# Revit family: ADSK_Фундамент_Монолитный_КолоннаМеталлическая_с_подливкой
name_source: partatom
category: Фундамент несущей конструкции
units: mm (PartAtom-declared; Revit-internal decimal feet)

## family parameters
Всегда вертикально = Да
Заглушка = Нет
Материал для поведения модели = Бетон
На основе рабочей плоскости = Нет
Общий = Нет
При загрузке вырезать с полостями = Нет

## types (5) — shared parameters
ADSK_Версия Revit = 2021
ADSK_Версия семейства = 1.1
ADSK_Масса элемента = 0.00 кг
ADSK_Основной материал элемента = Бетон
Материал несущих конструкций = <По категории>
Материал подливки = <По категории>
Подколонник_Ширина = 400 мм
Подливка = Да
ТВ1 = Болт фундаментный_Тип 1_ГОСТ 24379.1-2012
ТВ2 = Болт фундаментный_Тип 5_ГОСТ 24379.1-2012
Уступ 2_Высота = 200 мм
Уступ 3_Высота = 200 мм
zero-valued in all types: Толщина фундамента

## per-type parameters (varying)
| type | ADSK_Наименование | Длина | Плита_Количество уступов | Подколонник_Высота | Подколонник_Длина | Подливка_Длина | Подливка_ширина | Расч_Плита_Количество уступов | Расч_Уступ 2_Высота | Расч_Уступ 2_Длина | Расч_Уступ 2_Ширина | Расч_Уступ 3_Высота | Расч_Уступ 3_Длина | Расч_Уступ 3_Ширина | Смещение_Уступ 2 | Смещение_Уступ 3 | Уступ 1_Высота | Уступ 1_Длина | Уступ 1_Ширина | Уступ 2_Длина | Уступ 2_Ширина | Уступ 3_Длина | Уступ 3_Ширина | Ширина |
| Фундамент_3 уступа_Тип 1 | Фундамент с 3-мя уступами | 1200 мм | 3 | 500 мм | 400 мм | 330 мм | 280 мм | 3 | 200 мм | 1000 мм | 1000 мм | 200 мм | 800 мм | 800 мм | 200 мм | 200 мм | 200 мм | 1200 мм | 1200 мм | 1000 мм | 1000 мм | 800 мм | 800 мм | 1200 мм |
| Фундамент_2 уступа_Тип 1 | Фундамент с 2-мя уступами | 1200 мм | 2 | 500 мм | 400 мм | 330 мм | 280 мм | 2 | 200 мм | 1000 мм | 1000 мм | 200 мм | 1000 мм | 1000 мм | 200 мм | 0 мм | 300 мм | 1200 мм | 1200 мм | 1000 мм | 1000 мм | 800 мм | 800 мм | 1200 мм |
| Фундамент_1 уступ_Тип 1 | Фундамент с 1-м уступом | 800 мм | 1 | 500 мм | 400 мм | 330 мм | 280 мм | 1 | 300 мм | 800 мм | 800 мм | 300 мм | 800 мм | 800 мм | 0 мм | 0 мм | 300 мм | 800 мм | 800 мм | 1000 мм | 1000 мм | 800 мм | 800 мм | 800 мм |
| Фундамент_2 уступа_Тип 2 | Фундамент с 2-мя уступами | 1200 мм | 2 | 600 мм | 600 мм | 500 мм | 500 мм | 2 | 200 мм | 1000 мм | 800 мм | 200 мм | 1000 мм | 800 мм | 200 мм | 0 мм | 250 мм | 1200 мм | 1000 мм | 1000 мм | 800 мм | 800 мм | 600 мм | 1000 мм |
| Фундамент_2 уступа_Тип 3 | Фундамент с 2-мя уступами | 1200 мм | 2 | 600 мм | 900 мм | 330 мм | 280 мм | 2 | 200 мм | 1200 мм | 800 мм | 200 мм | 1200 мм | 800 мм | 200 мм | 0 мм | 250 мм | 1200 мм | 1000 мм | 1200 мм | 800 мм | 1000 мм | 600 мм | 1000 мм |
